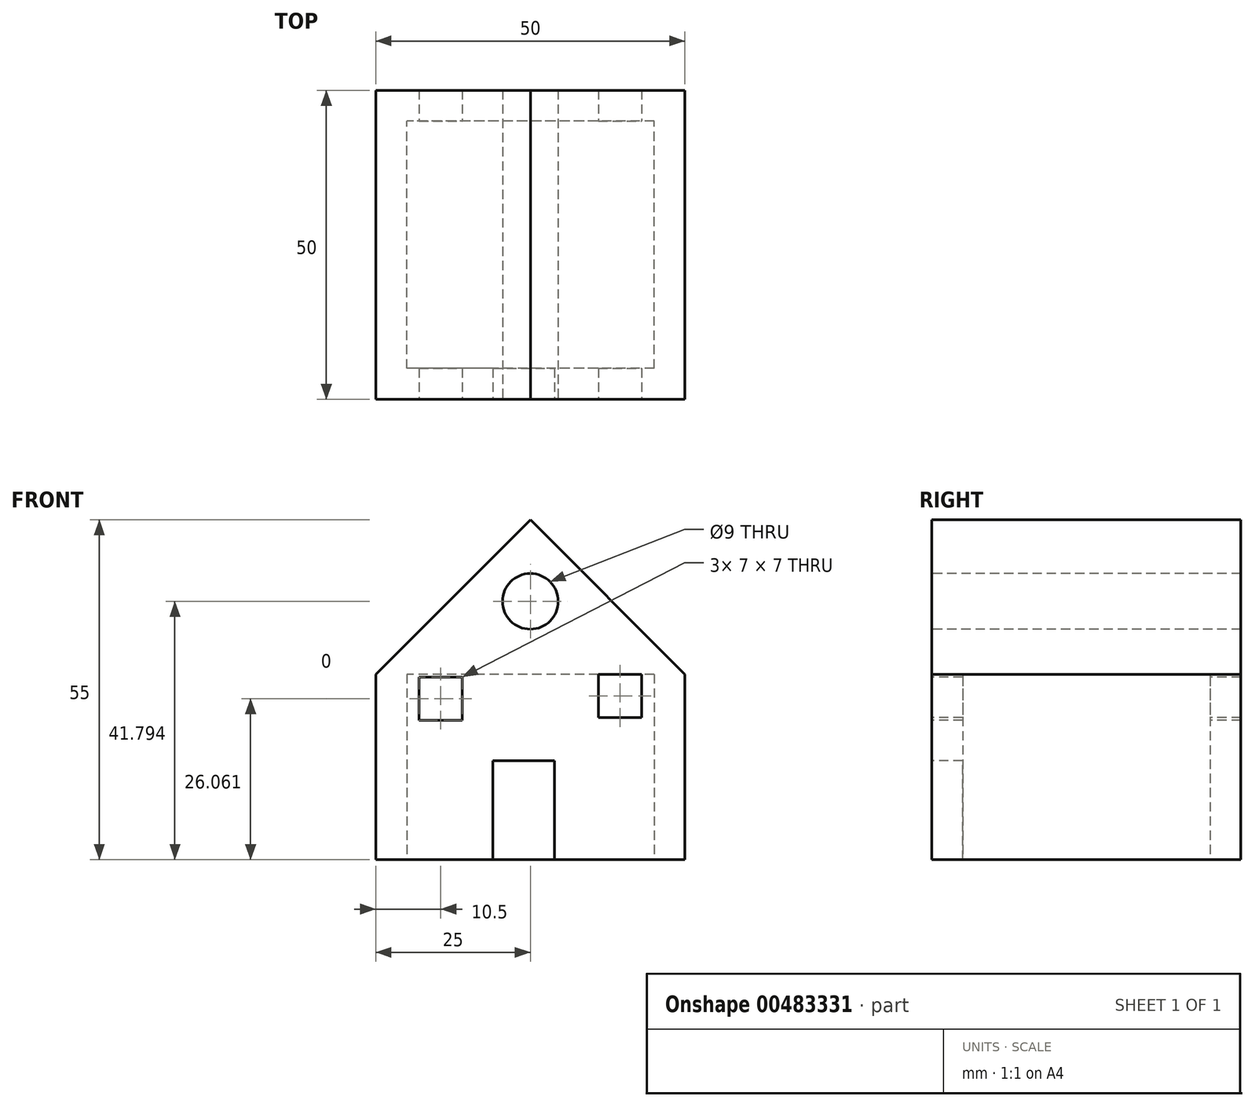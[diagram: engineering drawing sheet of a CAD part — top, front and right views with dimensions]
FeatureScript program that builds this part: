
annotation { "Feature Type Name" : "Feature", "Feature Type Description" : "" }
export const myFeature = defineFeature(function(context is Context, id is Id, definition is map)
    precondition{}
    {
        {
            var Q0;
            Q0=qCreatedBy(makeId("Top.planeOp"),FACE);
            var sketch = newSketch(context, id + "F0", { "sketchPlane" : qUnion([Q0])});
            skLineSegment(sketch, "E0.bottom", {"start": v(0, 0) * mm, "end": v(50, 0) * mm});
            skLineSegment(sketch, "E0.top", {"start": v(0, 50) * mm, "end": v(50, 50) * mm});
            skLineSegment(sketch, "E0.left", {"start": v(0, 0) * mm, "end": v(0, 50) * mm});
            skLineSegment(sketch, "E0.right", {"start": v(50, 0) * mm, "end": v(50, 50) * mm});
            skLineSegment(sketch, "E1.bottom", {"start": v(45, 5) * mm, "end": v(5, 5) * mm});
            skLineSegment(sketch, "E1.top", {"start": v(45, 45) * mm, "end": v(5, 45) * mm});
            skLineSegment(sketch, "E1.left", {"start": v(45, 5) * mm, "end": v(45, 45) * mm});
            skLineSegment(sketch, "E1.right", {"start": v(5, 5) * mm, "end": v(5, 45) * mm});
            skPoint(sketch, "E1.middle", {"position": v(25, 25) * mm});
            skLineSegment(sketch, "E2", {"start": v(25, 25) * mm, "end": v(25, 50) * mm, "construction": true});
            skLineSegment(sketch, "E3", {"start": v(25, 25) * mm, "end": v(0, 25) * mm, "construction": true});
            skSolve(sketch);
        }
        {
            var Q0;
            Q0=makeQuery(id+"F0.imprint","IMPRINT",FACE,{"disambiguationData":[TD([[makeQuery(id+"F0.imprint","IMPRINT",EDGE,{"derivedFrom":sQuery(id+"F0.wireOp",EDGE,"E0.bottom")}),1.0]])]});
            extrude(context, id + "F1", {"entities" : qUnion([Q0]), "depth" : 30 * mm});
        }
        {
            var Q0;
            Q0=makeQuery(id+"F1.opExtrude","CAP_FACE",FACE,{"disambiguationData":[OSD([sQuery(id+"F0.wireOp",EDGE,"E0.bottom"),sQuery(id+"F0.wireOp",EDGE,"E0.top"),sQuery(id+"F0.wireOp",EDGE,"E0.left"),sQuery(id+"F0.wireOp",EDGE,"E0.right"),sQuery(id+"F0.wireOp",EDGE,"E1.bottom"),sQuery(id+"F0.wireOp",EDGE,"E1.top"),sQuery(id+"F0.wireOp",EDGE,"E1.left"),sQuery(id+"F0.wireOp",EDGE,"E1.right")])],"isStart":false});
            var sketch = newSketch(context, id + "F2", { "sketchPlane" : qUnion([Q0])});
            skLineSegment(sketch, "E4.bottom", {"start": v(0, 0) * mm, "end": v(50, 0) * mm});
            skLineSegment(sketch, "E4.top", {"start": v(0, 50) * mm, "end": v(50, 50) * mm});
            skLineSegment(sketch, "E4.left", {"start": v(0, 0) * mm, "end": v(0, 50) * mm});
            skLineSegment(sketch, "E4.right", {"start": v(50, 0) * mm, "end": v(50, 50) * mm});
            skSolve(sketch);
        }
        {
            var Q0;
            Q0 = qSketchRegion(id + "F2", true);
            extrude(context, id + "F3", {"entities" : qUnion([Q0]), "operationType" : NewBodyOperationType.ADD, "depth" : 25 * mm});
        }
        {
            var Q0;
            Q0=makeQuery(id+"F3.opExtrude","CAP_EDGE",EDGE,{"disambiguationData":[OSD([sQuery(id+"F2.wireOp",EDGE,"E4.left")])],"isStart":false});
            var Q1;
            Q1=makeQuery(id+"F3.opExtrude","CAP_EDGE",EDGE,{"disambiguationData":[OSD([sQuery(id+"F2.wireOp",EDGE,"E4.right")])],"isStart":false});
            chamfer(context, id + "F4", {"entities" : qUnion([Q0, Q1]), "width" : 25 * mm, "tangentPropagation" : true});
        }
        {
            var Q0;
            Q0=makeQuery(id+"F3.boolean.opBoolean","MERGE",FACE,{"derivedFrom":[makeQuery(id+"F1.opExtrude","SWEPT_FACE",FACE,{"disambiguationData":[OSD([sQuery(id+"F0.wireOp",EDGE,"E0.bottom")])]}),makeQuery(id+"F3.opExtrude","SWEPT_FACE",FACE,{"disambiguationData":[OSD([sQuery(id+"F2.wireOp",EDGE,"E4.bottom")])]})]});
            var sketch = newSketch(context, id + "F5", { "sketchPlane" : qUnion([Q0])});
            skLineSegment(sketch, "E5.bottom", {"start": v(18.93, 0) * mm, "end": v(28.93, 0) * mm});
            skLineSegment(sketch, "E5.top", {"start": v(18.93, 16) * mm, "end": v(28.93, 16) * mm});
            skLineSegment(sketch, "E5.left", {"start": v(18.93, 0) * mm, "end": v(18.93, 16) * mm});
            skLineSegment(sketch, "E5.right", {"start": v(28.93, 0) * mm, "end": v(28.93, 16) * mm});
            skLineSegment(sketch, "E6.bottom", {"start": v(7, 29.56) * mm, "end": v(14, 29.56) * mm});
            skLineSegment(sketch, "E6.top", {"start": v(7, 22.56) * mm, "end": v(14, 22.56) * mm});
            skLineSegment(sketch, "E6.left", {"start": v(7, 29.56) * mm, "end": v(7, 22.56) * mm});
            skLineSegment(sketch, "E6.right", {"start": v(14, 29.56) * mm, "end": v(14, 22.56) * mm});
            skLineSegment(sketch, "E7.bottom", {"start": v(36, 30) * mm, "end": v(43, 30) * mm});
            skLineSegment(sketch, "E7.top", {"start": v(36, 23) * mm, "end": v(43, 23) * mm});
            skLineSegment(sketch, "E7.left", {"start": v(36, 30) * mm, "end": v(36, 23) * mm});
            skLineSegment(sketch, "E7.right", {"start": v(43, 30) * mm, "end": v(43, 23) * mm});
            skCircle(sketch, "E8", {"center": v(25, 41.8) * mm, "radius": 4.5 * mm});
            skLineSegment(sketch, "E9", {"start": v(7, 22.56) * mm, "end": v(0, 22.56) * mm, "construction": true});
            skLineSegment(sketch, "E10", {"start": v(43, 23) * mm, "end": v(50, 23) * mm, "construction": true});
            skSolve(sketch);
        }
        {
            var Q0;
            Q0=makeQuery(id+"F5.imprint","IMPRINT",FACE,{"disambiguationData":[TD([[makeQuery(id+"F5.imprint","IMPRINT",EDGE,{"derivedFrom":sQuery(id+"F5.wireOp",EDGE,"E5.bottom")}),1.0]])]});
            extrude(context, id + "F6", {"entities" : qUnion([Q0]), "operationType" : NewBodyOperationType.REMOVE, "oppositeDirection" : true, "depth" : 5 * mm});
        }
        {
            var Q0;
            Q0=makeQuery(id+"F5.imprint","IMPRINT",FACE,{"disambiguationData":[TD([[makeQuery(id+"F5.imprint","IMPRINT",EDGE,{"derivedFrom":sQuery(id+"F5.wireOp",EDGE,"E6.bottom")}),-1.0]])]});
            var Q1;
            Q1=makeQuery(id+"F5.imprint","IMPRINT",FACE,{"disambiguationData":[TD([[makeQuery(id+"F5.imprint","IMPRINT",EDGE,{"derivedFrom":sQuery(id+"F5.wireOp",EDGE,"E7.bottom")}),-1.0]])]});
            extrude(context, id + "F7", {"entities" : qUnion([Q0, Q1]), "operationType" : NewBodyOperationType.REMOVE, "endBound" : BoundingType.THROUGH_ALL, "oppositeDirection" : true, "depth" : 5 * mm});
        }
        {
            var Q0;
            Q0=makeQuery(id+"F5.imprint","IMPRINT",FACE,{"disambiguationData":[TD([[makeQuery(id+"F5.imprint","IMPRINT",EDGE,{"derivedFrom":sQuery(id+"F5.wireOp",EDGE,"E8")}),1.0]])]});
            extrude(context, id + "F8", {"entities" : qUnion([Q0]), "operationType" : NewBodyOperationType.REMOVE, "endBound" : BoundingType.THROUGH_ALL, "oppositeDirection" : true, "depth" : 25 * mm});
        }
    });
